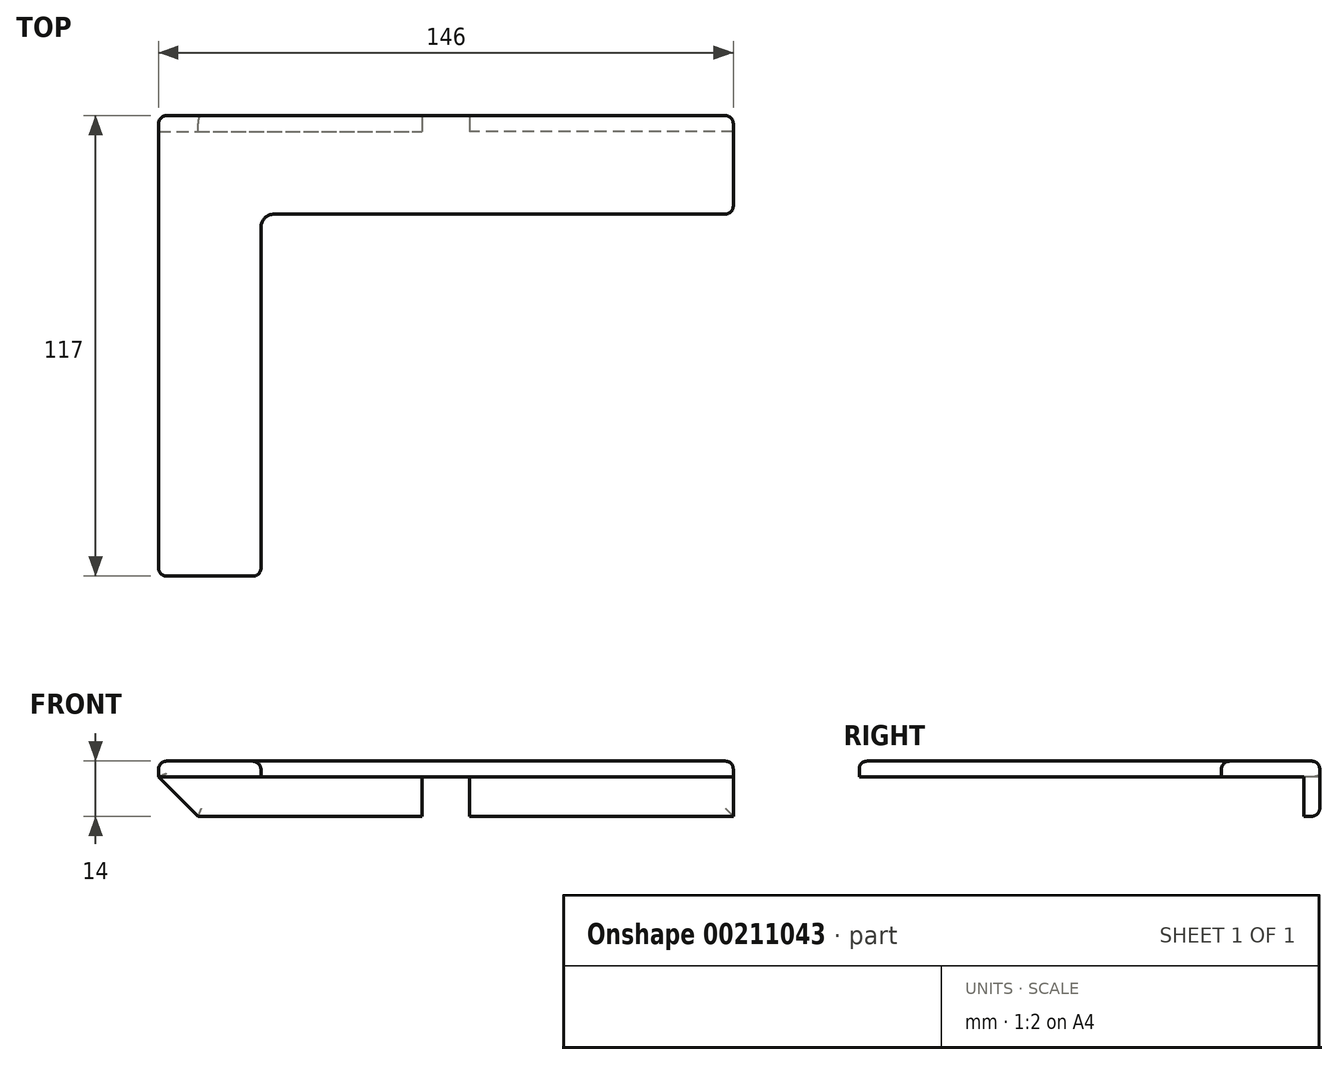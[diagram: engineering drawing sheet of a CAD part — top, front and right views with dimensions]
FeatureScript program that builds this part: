
annotation { "Feature Type Name" : "Feature", "Feature Type Description" : "" }
export const myFeature = defineFeature(function(context is Context, id is Id, definition is map)
    precondition{}
    {
        {
            var Q0;
            Q0=qCreatedBy(makeId("Top.planeOp"),FACE);
            var sketch = newSketch(context, id + "F0", { "sketchPlane" : qUnion([Q0])});
            skLineSegment(sketch, "E0.bottom", {"start": v(-108.82, 61.24) * mm, "end": v(37.18, 61.24) * mm});
            skLineSegment(sketch, "E0.top", {"start": v(-82.82, 36.24) * mm, "end": v(37.18, 36.24) * mm});
            skLineSegment(sketch, "E0.left", {"start": v(-108.82, 61.24) * mm, "end": v(-108.82, 36.24) * mm});
            skLineSegment(sketch, "E0.right", {"start": v(37.18, 61.24) * mm, "end": v(37.18, 36.24) * mm});
            skLineSegment(sketch, "E1.top", {"start": v(-108.82, -55.76) * mm, "end": v(-82.82, -55.76) * mm});
            skLineSegment(sketch, "E1.left", {"start": v(-108.82, 36.24) * mm, "end": v(-108.82, -55.76) * mm});
            skLineSegment(sketch, "E1.right", {"start": v(-82.82, 36.24) * mm, "end": v(-82.82, -55.76) * mm});
            skSolve(sketch);
        }
        {
            var Q0;
            Q0 = qSketchRegion(id + "F0", true);
            extrude(context, id + "F1", {"entities" : qUnion([Q0]), "depth" : 4 * mm});
        }
        {
            var Q0;
            Q0=makeQuery(id+"F1.opExtrude","CAP_FACE",FACE,{"disambiguationData":[OSD([sQuery(id+"F0.wireOp",EDGE,"E0.bottom"),sQuery(id+"F0.wireOp",EDGE,"E0.top"),sQuery(id+"F0.wireOp",EDGE,"E0.left"),sQuery(id+"F0.wireOp",EDGE,"E0.right"),sQuery(id+"F0.wireOp",EDGE,"E1.top"),sQuery(id+"F0.wireOp",EDGE,"E1.left"),sQuery(id+"F0.wireOp",EDGE,"E1.right")])],"isStart":true});
            var sketch = newSketch(context, id + "F2", { "sketchPlane" : qUnion([Q0])});
            skLineSegment(sketch, "E2.bottom", {"start": v(-108.82, -61.24) * mm, "end": v(-41.82, -61.24) * mm});
            skLineSegment(sketch, "E2.top", {"start": v(-108.82, -57.24) * mm, "end": v(-41.82, -57.24) * mm});
            skLineSegment(sketch, "E2.left", {"start": v(-108.82, -61.24) * mm, "end": v(-108.82, -57.24) * mm});
            skLineSegment(sketch, "E2.right", {"start": v(-41.82, -61.24) * mm, "end": v(-41.82, -57.24) * mm});
            skLineSegment(sketch, "E3.bottom", {"start": v(37.18, -61.24) * mm, "end": v(-29.82, -61.24) * mm});
            skLineSegment(sketch, "E3.top", {"start": v(37.18, -57.24) * mm, "end": v(-29.82, -57.24) * mm});
            skLineSegment(sketch, "E3.left", {"start": v(37.18, -61.24) * mm, "end": v(37.18, -57.24) * mm});
            skLineSegment(sketch, "E3.right", {"start": v(-29.82, -61.24) * mm, "end": v(-29.82, -57.24) * mm});
            skSolve(sketch);
        }
        {
            var Q0;
            Q0=makeQuery(id+"F2.imprint","IMPRINT",FACE,{"disambiguationData":[TD([[makeQuery(id+"F2.imprint","IMPRINT",EDGE,{"derivedFrom":sQuery(id+"F2.wireOp",EDGE,"E3.bottom")}),1.0]])]});
            var Q1;
            Q1=makeQuery(id+"F2.imprint","IMPRINT",FACE,{"disambiguationData":[TD([[makeQuery(id+"F2.imprint","IMPRINT",EDGE,{"derivedFrom":sQuery(id+"F2.wireOp",EDGE,"E2.bottom")}),1.0]])]});
            extrude(context, id + "F3", {"entities" : qUnion([Q0, Q1]), "operationType" : NewBodyOperationType.ADD, "depth" : 10 * mm});
        }
        {
            var Q0;
            Q0=makeQuery(id+"F1.opExtrude","SWEPT_EDGE",EDGE,{"disambiguationData":[OSD([sQuery(id+"F0.wireOp",EDGE,"E0.top"),sQuery(id+"F0.wireOp",EDGE,"E1.right")])]});
            fillet(context, id + "F4", {"entities" : qUnion([Q0]), "radius" : 3.38 * mm, "tangentPropagation" : true, "allowEdgeOverflow" : false});
        }
        {
            var Q0;
            Q0=makeQuery(id+"F1.opExtrude","CAP_EDGE",EDGE,{"disambiguationData":[OSD([sQuery(id+"F0.wireOp",EDGE,"E1.right")])],"isStart":false});
            var Q1;
            Q1=makeQuery(id+"F1.opExtrude","CAP_EDGE",EDGE,{"disambiguationData":[OSD([sQuery(id+"F0.wireOp",EDGE,"E0.top")])],"isStart":false});
            fillet(context, id + "F5", {"entities" : qUnion([Q0, Q1]), "radius" : 2.17 * mm, "allowEdgeOverflow" : false});
        }
        {
            var Q0;
            Q0=makeQuery(id+"F3.opExtrude","CAP_EDGE",EDGE,{"disambiguationData":[OSD([sQuery(id+"F2.wireOp",EDGE,"E2.left")])],"isStart":false});
            chamfer(context, id + "F6", {"entities" : qUnion([Q0]), "width" : 10 * mm, "tangentPropagation" : true});
        }
        {
            var Q0;
            Q0=makeQuery(id+"F6.opChamfer","BLEND_EDGE",EDGE,{"blendedFrom":[makeQuery(id+"F3.opExtrude","CAP_EDGE",EDGE,{"disambiguationData":[OSD([sQuery(id+"F2.wireOp",EDGE,"E2.left")])],"isStart":false}),makeQuery(id+"F3.boolean.opBoolean","MERGE",FACE,{"derivedFrom":[makeQuery(id+"F1.opExtrude","SWEPT_FACE",FACE,{"disambiguationData":[OSD([sQuery(id+"F0.wireOp",EDGE,"E0.bottom")])]}),makeQuery(id+"F3.opExtrude","SWEPT_FACE",FACE,{"disambiguationData":[OSD([sQuery(id+"F2.wireOp",EDGE,"E2.bottom")])]}),makeQuery(id+"F3.opExtrude","SWEPT_FACE",FACE,{"disambiguationData":[OSD([sQuery(id+"F2.wireOp",EDGE,"E3.bottom")])]})]})],"blendedInto":[makeQuery(id+"F3.boolean.opBoolean","MERGE",FACE,{"derivedFrom":[makeQuery(id+"F1.opExtrude","SWEPT_FACE",FACE,{"disambiguationData":[OSD([sQuery(id+"F0.wireOp",EDGE,"E0.bottom")])]}),makeQuery(id+"F3.opExtrude","SWEPT_FACE",FACE,{"disambiguationData":[OSD([sQuery(id+"F2.wireOp",EDGE,"E2.bottom")])]}),makeQuery(id+"F3.opExtrude","SWEPT_FACE",FACE,{"disambiguationData":[OSD([sQuery(id+"F2.wireOp",EDGE,"E3.bottom")])]})]})]});
            var Q1;
            Q1=makeQuery(id+"F1.opExtrude","CAP_EDGE",EDGE,{"disambiguationData":[OSD([sQuery(id+"F0.wireOp",EDGE,"E0.bottom")])],"isStart":false});
            var Q2;
            Q2=makeQuery(id+"F1.opExtrude","CAP_EDGE",EDGE,{"disambiguationData":[OSD([sQuery(id+"F0.wireOp",EDGE,"E0.left"),sQuery(id+"F0.wireOp",EDGE,"E1.left")])],"isStart":false});
            var Q3;
            Q3=makeQuery(id+"F3.boolean.opBoolean","MERGE",EDGE,{"derivedFrom":[makeQuery(id+"F1.opExtrude","SWEPT_EDGE",EDGE,{"disambiguationData":[OSD([sQuery(id+"F0.wireOp",EDGE,"E0.bottom"),sQuery(id+"F0.wireOp",EDGE,"E0.left")])]}),makeQuery(id+"F3.opExtrude","SWEPT_EDGE",EDGE,{"disambiguationData":[OSD([sQuery(id+"F2.wireOp",EDGE,"E2.bottom"),sQuery(id+"F2.wireOp",EDGE,"E2.left")])]})]});
            var Q4;
            Q4=makeQuery(id+"F3.boolean.opBoolean","MERGE",EDGE,{"derivedFrom":[makeQuery(id+"F1.opExtrude","SWEPT_EDGE",EDGE,{"disambiguationData":[OSD([sQuery(id+"F0.wireOp",EDGE,"E0.bottom"),sQuery(id+"F0.wireOp",EDGE,"E0.right")])]}),makeQuery(id+"F3.opExtrude","SWEPT_EDGE",EDGE,{"disambiguationData":[OSD([sQuery(id+"F2.wireOp",EDGE,"E3.bottom"),sQuery(id+"F2.wireOp",EDGE,"E3.left")])]})]});
            var Q5;
            Q5=makeQuery(id+"F3.opExtrude","CAP_EDGE",EDGE,{"disambiguationData":[OSD([sQuery(id+"F2.wireOp",EDGE,"E3.bottom")])],"isStart":false});
            var Q6;
            Q6=makeQuery(id+"F3.opExtrude","CAP_EDGE",EDGE,{"disambiguationData":[OSD([sQuery(id+"F2.wireOp",EDGE,"E2.bottom")])],"isStart":false});
            var Q7;
            Q7=makeQuery(id+"F1.opExtrude","CAP_EDGE",EDGE,{"disambiguationData":[OSD([sQuery(id+"F0.wireOp",EDGE,"E0.right")])],"isStart":false});
            fillet(context, id + "F7", {"entities" : qUnion([Q0, Q1, Q2, Q3, Q4, Q5, Q6, Q7]), "radius" : 2 * mm, "tangentPropagation" : true, "allowEdgeOverflow" : false});
        }
        {
            var Q0;
            Q0=makeQuery(id+"F1.opExtrude","CAP_EDGE",EDGE,{"disambiguationData":[OSD([sQuery(id+"F0.wireOp",EDGE,"E1.top")])],"isStart":false});
            fillet(context, id + "F8", {"entities" : qUnion([Q0]), "radius" : 2 * mm, "tangentPropagation" : true, "allowEdgeOverflow" : false});
        }
    });
